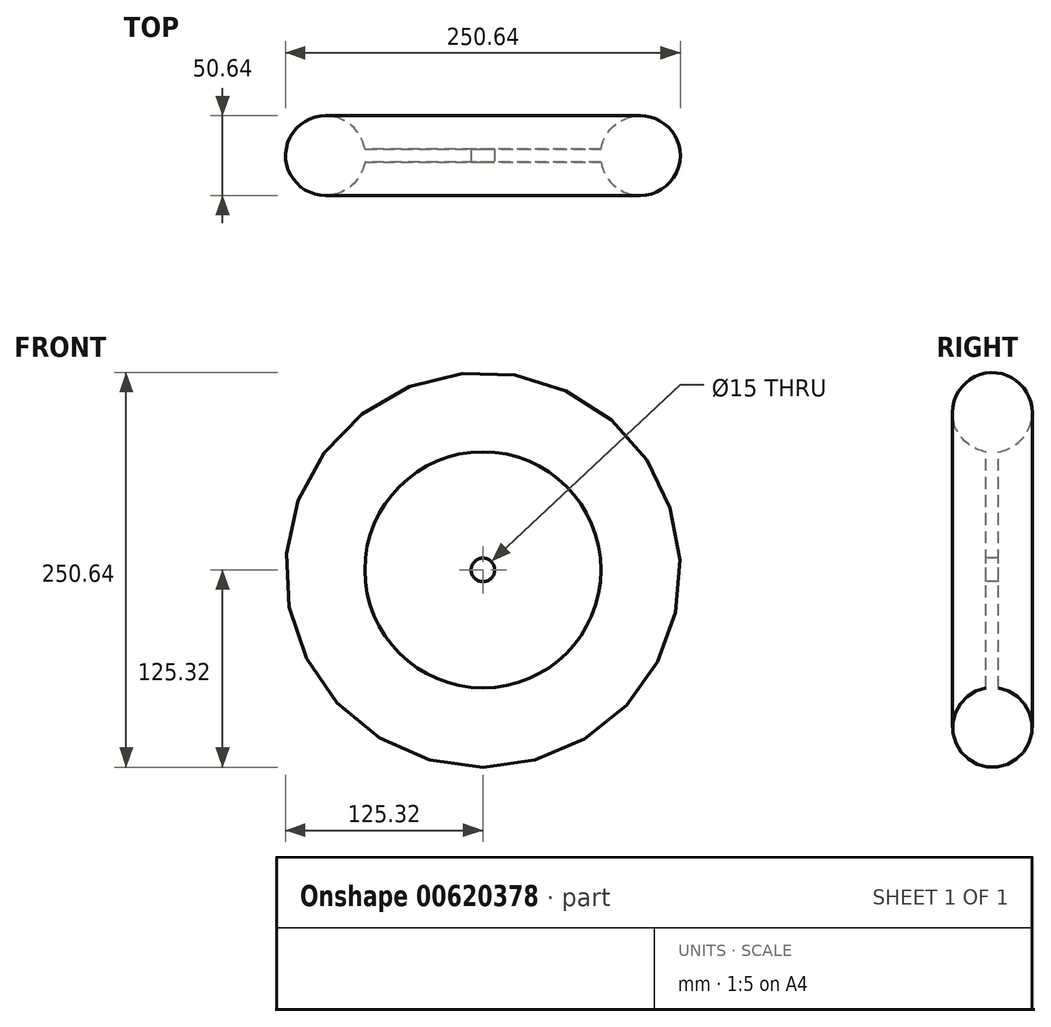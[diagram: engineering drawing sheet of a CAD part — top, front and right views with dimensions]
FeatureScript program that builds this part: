
annotation { "Feature Type Name" : "Feature", "Feature Type Description" : "" }
export const myFeature = defineFeature(function(context is Context, id is Id, definition is map)
    precondition{}
    {
        {
            var Q0;
            Q0=qCreatedBy(makeId("Right.planeOp"),FACE);
            var sketch = newSketch(context, id + "F0", { "sketchPlane" : qUnion([Q0])});
            skLineSegment(sketch, "E0", {"start": v(-23.79, 0) * mm, "end": v(27.48, 0) * mm, "construction": true});
            skLineSegment(sketch, "E1", {"start": v(-4, 7.5) * mm, "end": v(4, 7.5) * mm});
            skLineSegment(sketch, "E2", {"start": v(4, 7.5) * mm, "end": v(4, 75) * mm});
            skLineSegment(sketch, "E3", {"start": v(-4, 7.5) * mm, "end": v(-4, 75) * mm});
            skArc(sketch, "E4", {"start": v(4, 75) * mm, "mid": v(0, 125.32) * mm, "end": v(-4, 75) * mm});
            skSolve(sketch);
        }
        {
            var Q0;
            Q0 = qSketchRegion(id + "F0", true);
            var Q1;
            Q1=sQuery(id+"F0.wireOp",EDGE,"E0");
            revolve(context, id + "F1", {"surfaceOperationType" : NewSurfaceOperationType.NEW, "entities" : qUnion([Q0]), "axis" : qUnion([Q1]), "revolveType" : RevolveType.FULL});
        }
    });
